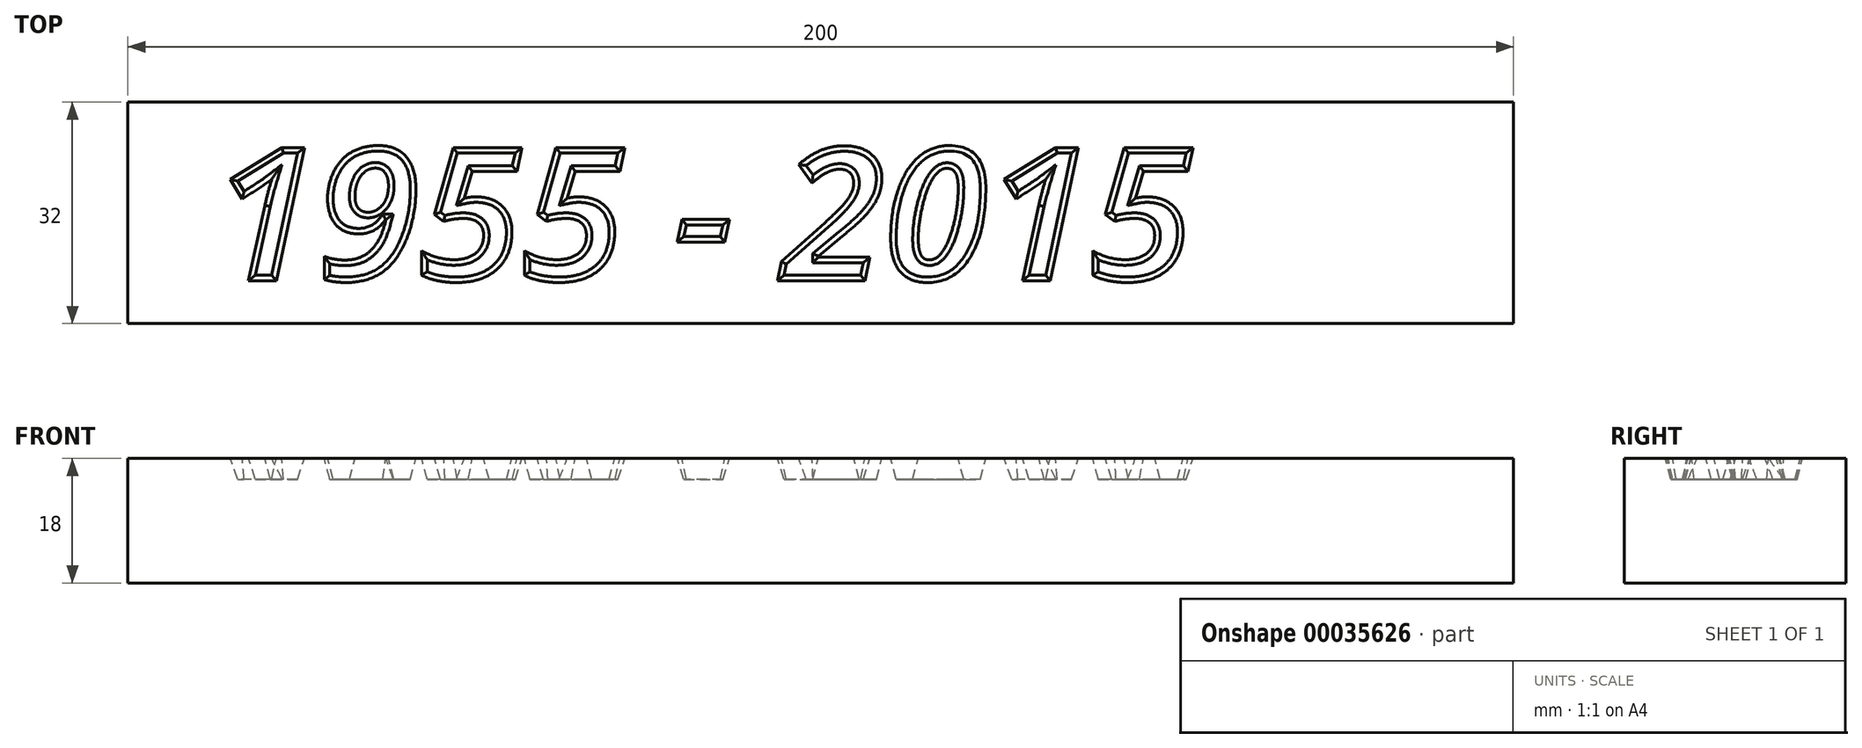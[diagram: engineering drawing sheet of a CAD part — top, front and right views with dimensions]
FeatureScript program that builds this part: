
annotation { "Feature Type Name" : "Feature", "Feature Type Description" : "" }
export const myFeature = defineFeature(function(context is Context, id is Id, definition is map)
    precondition{}
    {
        {
            var Q0;
            Q0=qCreatedBy(makeId("Top.planeOp"),FACE);
            var sketch = newSketch(context, id + "F0", { "sketchPlane" : qUnion([Q0])});
            skLineSegment(sketch, "E0.bottom", {"start": v(0, 0) * mm, "end": v(200, 0) * mm});
            skLineSegment(sketch, "E0.top", {"start": v(0, 32) * mm, "end": v(200, 32) * mm});
            skLineSegment(sketch, "E0.left", {"start": v(0, 0) * mm, "end": v(0, 32) * mm});
            skLineSegment(sketch, "E0.right", {"start": v(200, 0) * mm, "end": v(200, 32) * mm});
            skSolve(sketch);
        }
        {
            var Q0;
            Q0=makeQuery(id+"F0.imprint","IMPRINT",FACE,{"disambiguationData":[TD([[makeQuery(id+"F0.imprint","IMPRINT",EDGE,{"derivedFrom":sQuery(id+"F0.wireOp",EDGE,"E0.bottom")}),1.0]])]});
            extrude(context, id + "F1", {"entities" : qUnion([Q0]), "depth" : 18 * mm});
        }
        {
            var Q0;
            Q0=makeQuery(id+"F1.opExtrude","CAP_FACE",FACE,{"disambiguationData":[OSD([sQuery(id+"F0.wireOp",EDGE,"E0.bottom"),sQuery(id+"F0.wireOp",EDGE,"E0.top"),sQuery(id+"F0.wireOp",EDGE,"E0.left"),sQuery(id+"F0.wireOp",EDGE,"E0.right")])],"isStart":false});
            var sketch = newSketch(context, id + "F2", { "sketchPlane" : qUnion([Q0])});
            skText(sketch, "E1", { "text": "1955 - 2015", "fontName": "OpenSans-BoldItalic.ttf"});
            const initialGuessF2  = {"E1": [0.01236, 0.00619, 1, 0, 0.0194]};
            skSetInitialGuess(sketch, initialGuessF2);
            skSolve(sketch);
        }
        {
            var Q0;
            Q0 = qSketchRegion(id + "F2", true);
            extrude(context, id + "F3", {"entities" : qUnion([Q0]), "operationType" : NewBodyOperationType.REMOVE, "oppositeDirection" : true, "depth" : 3 * mm, "hasDraft" : true, "draftAngle" : 15 * degree, "draftPullDirection" : true});
        }
    });
